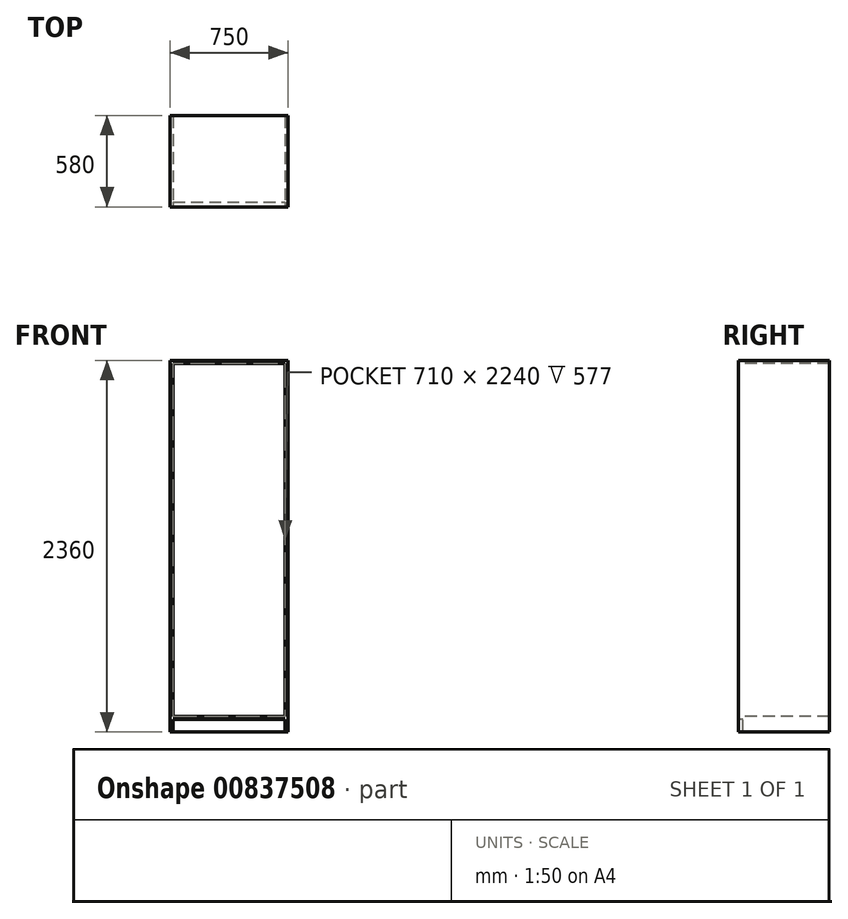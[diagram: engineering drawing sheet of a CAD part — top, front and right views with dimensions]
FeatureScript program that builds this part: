
annotation { "Feature Type Name" : "Feature", "Feature Type Description" : "" }
export const myFeature = defineFeature(function(context is Context, id is Id, definition is map)
    precondition{}
    {
        {
            var Q0;
            Q0=qCreatedBy(makeId("Front.planeOp"),FACE);
            var sketch = newSketch(context, id + "F0", { "sketchPlane" : qUnion([Q0])});
            skLineSegment(sketch, "E0.bottom", {"start": v(-375, 0) * mm, "end": v(375, 0) * mm});
            skLineSegment(sketch, "E0.top", {"start": v(-375, 2360) * mm, "end": v(375, 2360) * mm});
            skLineSegment(sketch, "E0.left", {"start": v(-375, 0) * mm, "end": v(-375, 2360) * mm});
            skLineSegment(sketch, "E0.right", {"start": v(375, 0) * mm, "end": v(375, 2360) * mm});
            skLineSegment(sketch, "E1", {"start": v(0, 2360) * mm, "end": v(0, 0) * mm, "construction": true});
            skSolve(sketch);
        }
        {
            var Q0;
            Q0=makeQuery(id+"F0.imprint","IMPRINT",FACE,{"disambiguationData":[TD([[makeQuery(id+"F0.imprint","IMPRINT",EDGE,{"derivedFrom":sQuery(id+"F0.wireOp",EDGE,"E0.bottom")}),1.0]])]});
            extrude(context, id + "F1", {"entities" : qUnion([Q0]), "depth" : 580 * mm, "offsetDistance" : 25 * mm});
        }
        {
            var Q0;
            Q0=makeQuery(id+"F1.opExtrude","CAP_FACE",FACE,{"disambiguationData":[OSD([sQuery(id+"F0.wireOp",EDGE,"E0.bottom"),sQuery(id+"F0.wireOp",EDGE,"E0.top"),sQuery(id+"F0.wireOp",EDGE,"E0.left"),sQuery(id+"F0.wireOp",EDGE,"E0.right")])],"isStart":false});
            var sketch = newSketch(context, id + "F2", { "sketchPlane" : qUnion([Q0])});
            skLineSegment(sketch, "E2.bottom", {"start": v(-355, 2340) * mm, "end": v(355, 2340) * mm});
            skLineSegment(sketch, "E2.top", {"start": v(-355, 100) * mm, "end": v(355, 100) * mm});
            skLineSegment(sketch, "E2.left", {"start": v(-355, 2340) * mm, "end": v(-355, 100) * mm});
            skLineSegment(sketch, "E2.right", {"start": v(355, 2340) * mm, "end": v(355, 100) * mm});
            skLineSegment(sketch, "E3.bottom", {"start": v(355, 2340) * mm, "end": v(375, 2340) * mm, "construction": true});
            skLineSegment(sketch, "E3.top", {"start": v(355, 2360) * mm, "end": v(375, 2360) * mm, "construction": true});
            skLineSegment(sketch, "E3.left", {"start": v(355, 2340) * mm, "end": v(355, 2360) * mm, "construction": true});
            skLineSegment(sketch, "E3.right", {"start": v(375, 2340) * mm, "end": v(375, 2360) * mm, "construction": true});
            skLineSegment(sketch, "E4.bottom", {"start": v(-355, 2340) * mm, "end": v(-375, 2340) * mm, "construction": true});
            skLineSegment(sketch, "E4.top", {"start": v(-355, 2360) * mm, "end": v(-375, 2360) * mm, "construction": true});
            skLineSegment(sketch, "E4.left", {"start": v(-355, 2340) * mm, "end": v(-355, 2360) * mm, "construction": true});
            skLineSegment(sketch, "E4.right", {"start": v(-375, 2340) * mm, "end": v(-375, 2360) * mm, "construction": true});
            skSolve(sketch);
        }
        {
            var Q0;
            Q0=makeQuery(id+"F1.opExtrude","CAP_FACE",FACE,{"disambiguationData":[OSD([sQuery(id+"F0.wireOp",EDGE,"E0.bottom"),sQuery(id+"F0.wireOp",EDGE,"E0.top"),sQuery(id+"F0.wireOp",EDGE,"E0.left"),sQuery(id+"F0.wireOp",EDGE,"E0.right")])],"isStart":true});
            cPlane(context, id + "F3", {"entities" : qUnion([Q0]), "cplaneType" : CPlaneType.OFFSET, "offset" : 3 * mm, "oppositeDirection" : true, "width" : 150 * mm, "height" : 150 * mm});
        }
        {
            var Q0;
            Q0=makeQuery(id+"F2.imprint","IMPRINT",FACE,{"disambiguationData":[TD([[makeQuery(id+"F2.imprint","IMPRINT",EDGE,{"derivedFrom":sQuery(id+"F2.wireOp",EDGE,"E2.bottom")}),-1.0]])]});
            var Q1;
            Q1=qCreatedBy(id+"F3.planeOp",FACE);
            extrude(context, id + "F4", {"entities" : qUnion([Q0]), "operationType" : NewBodyOperationType.REMOVE, "endBound" : BoundingType.UP_TO_SURFACE, "oppositeDirection" : true, "depth" : 25 * mm, "endBoundEntityFace" : qUnion([Q1]), "offsetDistance" : 25 * mm});
        }
        {
            var Q0;
            Q0=makeQuery(id+"F1.opExtrude","CAP_FACE",FACE,{"disambiguationData":[OSD([sQuery(id+"F0.wireOp",EDGE,"E0.bottom"),sQuery(id+"F0.wireOp",EDGE,"E0.top"),sQuery(id+"F0.wireOp",EDGE,"E0.left"),sQuery(id+"F0.wireOp",EDGE,"E0.right")])],"isStart":false});
            var sketch = newSketch(context, id + "F5", { "sketchPlane" : qUnion([Q0])});
            skLineSegment(sketch, "E5.bottom", {"start": v(-355, 0) * mm, "end": v(355, 0) * mm});
            skLineSegment(sketch, "E5.top", {"start": v(-355, 80) * mm, "end": v(355, 80) * mm});
            skLineSegment(sketch, "E5.left", {"start": v(-355, 0) * mm, "end": v(-355, 80) * mm});
            skLineSegment(sketch, "E5.right", {"start": v(355, 0) * mm, "end": v(355, 80) * mm});
            skLineSegment(sketch, "E6", {"start": v(355, 100) * mm, "end": v(355, 80) * mm, "construction": true});
            skLineSegment(sketch, "E7", {"start": v(355, 0) * mm, "end": v(375, 0) * mm, "construction": true});
            skSolve(sketch);
        }
        {
            var Q0;
            Q0=makeQuery(id+"F5.imprint","IMPRINT",FACE,{"disambiguationData":[TD([[makeQuery(id+"F5.imprint","IMPRINT",EDGE,{"derivedFrom":sQuery(id+"F5.wireOp",EDGE,"E5.bottom")}),1.0]])]});
            extrude(context, id + "F6", {"entities" : qUnion([Q0]), "operationType" : NewBodyOperationType.REMOVE, "oppositeDirection" : true, "depth" : 30 * mm, "offsetDistance" : 25 * mm});
        }
    });
